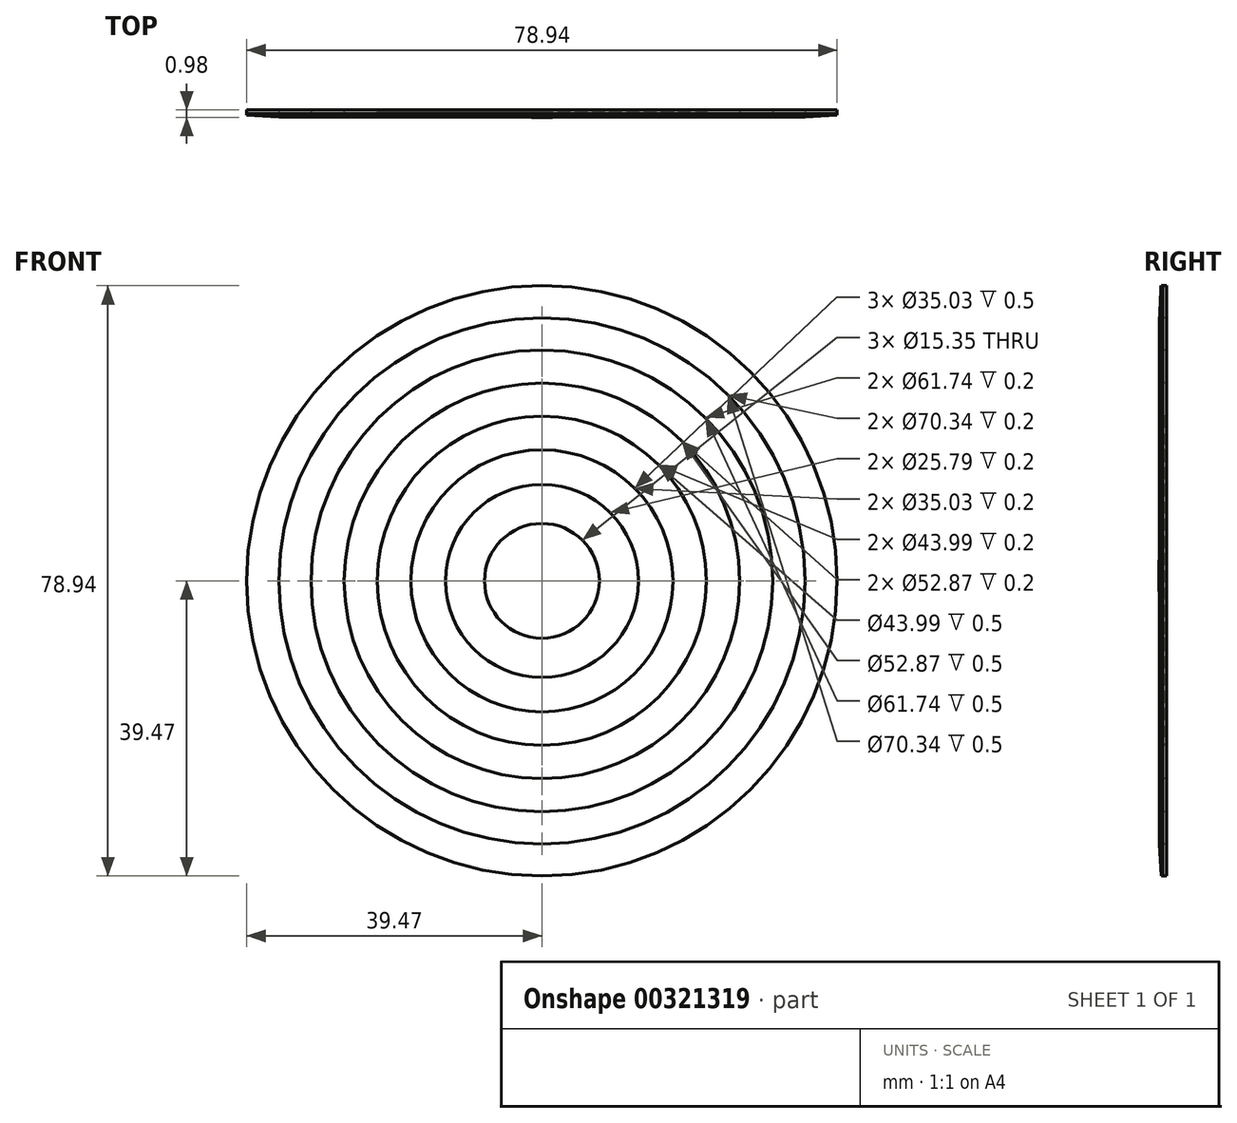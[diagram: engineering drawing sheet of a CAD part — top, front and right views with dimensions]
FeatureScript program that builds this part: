
annotation { "Feature Type Name" : "Feature", "Feature Type Description" : "" }
export const myFeature = defineFeature(function(context is Context, id is Id, definition is map)
    precondition{}
    {
        {
            var Q0;
            Q0=qCreatedBy(makeId("Top.planeOp"),FACE);
            var sketch = newSketch(context, id + "F0", { "sketchPlane" : qUnion([Q0])});
            skLineSegment(sketch, "E0", {"start": v(0, 0) * mm, "end": v(0, -0.27) * mm});
            skLineSegment(sketch, "E1", {"start": v(0, 0) * mm, "end": v(-10.49, 0) * mm});
            skLineSegment(sketch, "E2", {"start": v(0, 0) * mm, "end": v(7.68, 0) * mm});
            skArc(sketch, "E3", {"start": v(-10.49, 0) * mm, "mid": v(-1.4, -0.28) * mm, "end": v(7.68, 0) * mm});
            skLineSegment(sketch, "E4", {"start": v(7.68, 0) * mm, "end": v(12.9, 0) * mm});
            skLineSegment(sketch, "E5", {"start": v(7.68, 0) * mm, "end": v(7.68, -0.2) * mm});
            skLineSegment(sketch, "E6", {"start": v(12.9, 0) * mm, "end": v(17.52, 0) * mm});
            skLineSegment(sketch, "E7", {"start": v(17.52, 0) * mm, "end": v(22, 0) * mm});
            skLineSegment(sketch, "E8", {"start": v(22, 0) * mm, "end": v(26.44, 0) * mm});
            skLineSegment(sketch, "E9", {"start": v(26.44, 0) * mm, "end": v(30.87, 0) * mm});
            skLineSegment(sketch, "E10", {"start": v(12.9, 0) * mm, "end": v(12.9, -0.2) * mm});
            skLineSegment(sketch, "E11", {"start": v(17.52, 0) * mm, "end": v(17.52, -0.2) * mm});
            skLineSegment(sketch, "E12", {"start": v(22, 0) * mm, "end": v(22, -0.2) * mm});
            skLineSegment(sketch, "E13", {"start": v(26.44, 0) * mm, "end": v(26.44, -0.2) * mm});
            skLineSegment(sketch, "E14", {"start": v(30.87, 0) * mm, "end": v(30.87, -0.2) * mm});
            skLineSegment(sketch, "E15", {"start": v(7.67, -0.2) * mm, "end": v(12.9, 0) * mm});
            skLineSegment(sketch, "E16", {"start": v(12.9, -0.2) * mm, "end": v(17.52, 0) * mm});
            skLineSegment(sketch, "E17", {"start": v(17.52, -0.2) * mm, "end": v(22, 0) * mm});
            skLineSegment(sketch, "E18", {"start": v(22, -0.2) * mm, "end": v(26.44, 0) * mm});
            skLineSegment(sketch, "E19", {"start": v(26.44, -0.2) * mm, "end": v(30.87, 0) * mm});
            skLineSegment(sketch, "E20", {"start": v(30.87, 0) * mm, "end": v(35.17, 0) * mm});
            skLineSegment(sketch, "E21", {"start": v(35.17, 0) * mm, "end": v(35.17, -0.2) * mm});
            skLineSegment(sketch, "E22", {"start": v(30.87, -0.2) * mm, "end": v(35.17, 0) * mm});
            skLineSegment(sketch, "E23", {"start": v(35.17, 0) * mm, "end": v(39.47, 0) * mm});
            skLineSegment(sketch, "E24", {"start": v(39.47, 0) * mm, "end": v(35.17, -0.2) * mm});
            skSolve(sketch);
        }
        {
            var Q0;
            Q0=makeQuery(id+"F0.imprint","IMPRINT",FACE,{"disambiguationData":[TD([[makeQuery(id+"F0.imprint","IMPRINT",EDGE,{"derivedFrom":sQuery(id+"F0.wireOp",EDGE,"E4")}),-1.0]])]});
            var Q1;
            Q1=makeQuery(id+"F0.imprint","IMPRINT",FACE,{"disambiguationData":[TD([[makeQuery(id+"F0.imprint","IMPRINT",EDGE,{"derivedFrom":sQuery(id+"F0.wireOp",EDGE,"E6")}),-1.0]])]});
            var Q2;
            Q2=makeQuery(id+"F0.imprint","IMPRINT",FACE,{"disambiguationData":[TD([[makeQuery(id+"F0.imprint","IMPRINT",EDGE,{"derivedFrom":sQuery(id+"F0.wireOp",EDGE,"E7")}),-1.0]])]});
            var Q3;
            Q3=makeQuery(id+"F0.imprint","IMPRINT",FACE,{"disambiguationData":[TD([[makeQuery(id+"F0.imprint","IMPRINT",EDGE,{"derivedFrom":sQuery(id+"F0.wireOp",EDGE,"E8")}),-1.0]])]});
            var Q4;
            Q4=makeQuery(id+"F0.imprint","IMPRINT",FACE,{"disambiguationData":[TD([[makeQuery(id+"F0.imprint","IMPRINT",EDGE,{"derivedFrom":sQuery(id+"F0.wireOp",EDGE,"E9")}),-1.0]])]});
            var Q5;
            Q5=makeQuery(id+"F0.imprint","IMPRINT",FACE,{"disambiguationData":[TD([[makeQuery(id+"F0.imprint","IMPRINT",EDGE,{"derivedFrom":sQuery(id+"F0.wireOp",EDGE,"E14")}),1.0]])]});
            var Q6;
            Q6=makeQuery(id+"F0.imprint","IMPRINT",FACE,{"disambiguationData":[TD([[makeQuery(id+"F0.imprint","IMPRINT",EDGE,{"derivedFrom":sQuery(id+"F0.wireOp",EDGE,"E21")}),1.0]])]});
            var Q7;
            {var subQ0=sQuery(id+"F0.wireOp",EDGE,"E0");Q7=makeQuery(id+"F0.imprint","IMPRINT",FACE,{"disambiguationData":[TD([[makeQuery(id+"F0.imprint","IMPRINT",EDGE,{"derivedFrom":subQ0}),1.0]])]});}
            var Q8;
            Q8=sQuery(id+"F0.wireOp",EDGE,"E0");
            revolve(context, id + "F1", {"entities" : qUnion([Q0, Q1, Q2, Q3, Q4, Q5, Q6, Q7]), "axis" : qUnion([Q8]), "revolveType" : RevolveType.FULL});
        }
        {
            var Q0;
            Q0=makeQuery(id+"F1.opRevolve","SWEPT_FACE",FACE,{"disambiguationData":[OSD([sQuery(id+"F0.wireOp",EDGE,"E2")])]});
            var Q1;
            Q1=makeQuery(id+"F1.opRevolve","SWEPT_FACE",FACE,{"disambiguationData":[OSD([sQuery(id+"F0.wireOp",EDGE,"E4")])]});
            var Q2;
            Q2=makeQuery(id+"F1.opRevolve","SWEPT_FACE",FACE,{"disambiguationData":[OSD([sQuery(id+"F0.wireOp",EDGE,"E6")])]});
            var Q3;
            Q3=makeQuery(id+"F1.opRevolve","SWEPT_FACE",FACE,{"disambiguationData":[OSD([sQuery(id+"F0.wireOp",EDGE,"E7")])]});
            var Q4;
            Q4=makeQuery(id+"F1.opRevolve","SWEPT_FACE",FACE,{"disambiguationData":[OSD([sQuery(id+"F0.wireOp",EDGE,"E8")])]});
            var Q5;
            Q5=makeQuery(id+"F1.opRevolve","SWEPT_FACE",FACE,{"disambiguationData":[OSD([sQuery(id+"F0.wireOp",EDGE,"E9")])]});
            var Q6;
            Q6=makeQuery(id+"F1.opRevolve","SWEPT_FACE",FACE,{"disambiguationData":[OSD([sQuery(id+"F0.wireOp",EDGE,"E20")])]});
            var Q7;
            Q7=makeQuery(id+"F1.opRevolve","SWEPT_FACE",FACE,{"disambiguationData":[OSD([sQuery(id+"F0.wireOp",EDGE,"E23")])]});
            extrude(context, id + "F2", {"entities" : qUnion([Q0, Q1, Q2, Q3, Q4, Q5, Q6, Q7]), "depth" : .2 * mm});
        }
        {
            var Q0;
            Q0=makeQuery(id+"F2.opExtrude","CAP_FACE",FACE,{"disambiguationData":[OSD([sQuery(id+"F0.wireOp",EDGE,"E23")])],"isStart":false});
            var Q1;
            Q1=makeQuery(id+"F2.opExtrude","CAP_FACE",FACE,{"disambiguationData":[OSD([sQuery(id+"F0.wireOp",EDGE,"E2")])],"isStart":false});
            var Q2;
            Q2=makeQuery(id+"F2.opExtrude","CAP_FACE",FACE,{"disambiguationData":[OSD([sQuery(id+"F0.wireOp",EDGE,"E4")])],"isStart":false});
            var Q3;
            Q3=makeQuery(id+"F2.opExtrude","CAP_FACE",FACE,{"disambiguationData":[OSD([sQuery(id+"F0.wireOp",EDGE,"E7")])],"isStart":false});
            var Q4;
            Q4=makeQuery(id+"F2.opExtrude","CAP_FACE",FACE,{"disambiguationData":[OSD([sQuery(id+"F0.wireOp",EDGE,"E7")])],"isStart":true});
            var Q5;
            Q5=makeQuery(id+"F1.opRevolve","SWEPT_FACE",FACE,{"disambiguationData":[OSD([sQuery(id+"F0.wireOp",EDGE,"E7")])]});
            var Q6;
            Q6=makeQuery(id+"F2.opExtrude","CAP_FACE",FACE,{"disambiguationData":[OSD([sQuery(id+"F0.wireOp",EDGE,"E9")])],"isStart":false});
            var Q7;
            Q7=makeQuery(id+"F2.opExtrude","CAP_FACE",FACE,{"disambiguationData":[OSD([sQuery(id+"F0.wireOp",EDGE,"E20")])],"isStart":false});
            var Q8;
            Q8=makeQuery(id+"F2.opExtrude","CAP_FACE",FACE,{"disambiguationData":[OSD([sQuery(id+"F0.wireOp",EDGE,"E6")])],"isStart":false});
            var Q9;
            Q9=makeQuery(id+"F2.opExtrude","CAP_FACE",FACE,{"disambiguationData":[OSD([sQuery(id+"F0.wireOp",EDGE,"E8")])],"isStart":false});
            extrude(context, id + "F3", {"entities" : qUnion([Q0, Q1, Q2, Q3, Q4, Q5, Q6, Q7, Q8, Q9]), "depth" : 0.5 * mm, "offsetDistance" : 25 * mm});
        }
    });
